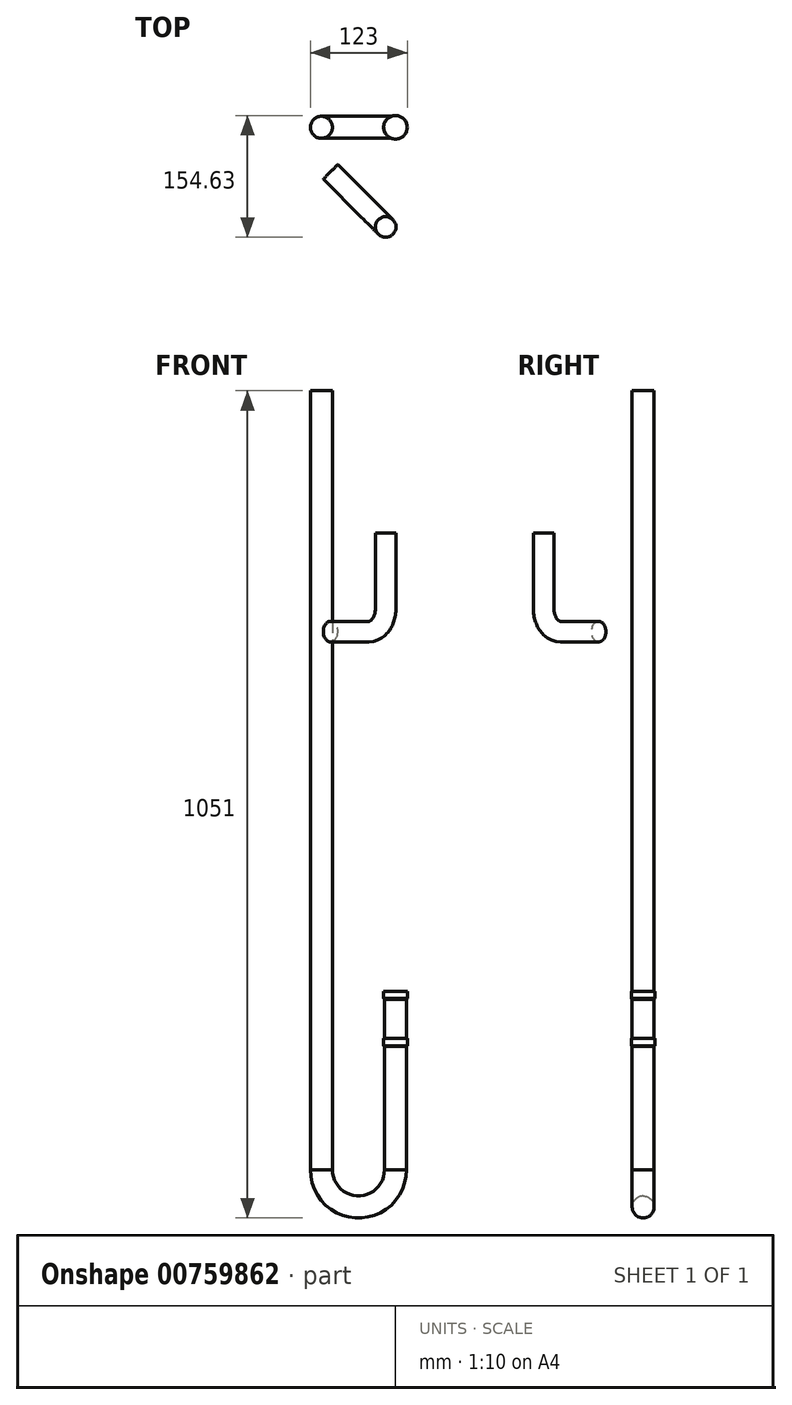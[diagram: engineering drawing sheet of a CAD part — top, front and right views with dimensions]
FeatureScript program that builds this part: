
annotation { "Feature Type Name" : "Feature", "Feature Type Description" : "" }
export const myFeature = defineFeature(function(context is Context, id is Id, definition is map)
    precondition{}
    {
        {
            var Q0;
            Q0=qCreatedBy(makeId("Top.planeOp"),FACE);
            cPlane(context, id + "F0", {"entities" : qUnion([Q0]), "cplaneType" : CPlaneType.OFFSET, "offset" : 302 * mm, "width" : 150 * mm, "height" : 150 * mm});
        }
        {
            var Q0;
            Q0=qCreatedBy(id+"F0.planeOp",FACE);
            var sketch = newSketch(context, id + "F1", { "sketchPlane" : qUnion([Q0])});
            skCircle(sketch, "E0", {"center": v(0, 0) * mm, "radius": 10 * mm});
            skSolve(sketch);
        }
        {
            var Q0;
            Q0=qCreatedBy(makeId("Front.planeOp"),FACE);
            var sketch = newSketch(context, id + "F2", { "sketchPlane" : qUnion([Q0])});
            skPoint(sketch, "E1.0", {"position": v(0, 302) * mm});
            skLineSegment(sketch, "E2", {"start": v(0, 302) * mm, "end": v(0, 75) * mm, "construction": true});
            skLineSegment(sketch, "E3", {"start": v(0, 75) * mm, "end": v(14, 75) * mm});
            skLineSegment(sketch, "E4", {"start": v(14, 75) * mm, "end": v(14, 232) * mm});
            skLineSegment(sketch, "E5", {"start": v(14, 232) * mm, "end": v(15, 232) * mm});
            skLineSegment(sketch, "E6", {"start": v(15, 232) * mm, "end": v(15, 242) * mm});
            skLineSegment(sketch, "E7", {"start": v(15, 242) * mm, "end": v(14, 242) * mm});
            skLineSegment(sketch, "E8", {"start": v(14, 242) * mm, "end": v(14, 292) * mm});
            skLineSegment(sketch, "E9", {"start": v(14, 292) * mm, "end": v(15, 292) * mm});
            skLineSegment(sketch, "E10", {"start": v(15, 292) * mm, "end": v(15, 302) * mm});
            skLineSegment(sketch, "E11", {"start": v(15, 302) * mm, "end": v(0, 302) * mm});
            skLineSegment(sketch, "E12", {"start": v(0, 75) * mm, "end": v(0, 302) * mm});
            skSolve(sketch);
        }
        {
            var Q0;
            Q0=makeQuery(id+"F2.imprint","IMPRINT",FACE,{"disambiguationData":[TD([[makeQuery(id+"F2.imprint","IMPRINT",EDGE,{"derivedFrom":sQuery(id+"F2.wireOp",EDGE,"E3")}),1.0]])]});
            var Q1;
            Q1=sQuery(id+"F2.wireOp",EDGE,"E12");
            revolve(context, id + "F3", {"surfaceOperationType" : NewSurfaceOperationType.NEW, "entities" : qUnion([Q0]), "axis" : qUnion([Q1]), "revolveType" : RevolveType.FULL});
        }
        {
            var Q0;
            Q0=makeQuery(id+"F3.opRevolve","SWEPT_EDGE",EDGE,{"disambiguationData":[OSD([sQuery(id+"F2.wireOp",EDGE,"E5"),sQuery(id+"F2.wireOp",EDGE,"E6")])]});
            var Q1;
            Q1=makeQuery(id+"F3.opRevolve","SWEPT_EDGE",EDGE,{"disambiguationData":[OSD([sQuery(id+"F2.wireOp",EDGE,"E9"),sQuery(id+"F2.wireOp",EDGE,"E10")])]});
            chamfer(context, id + "F4", {"entities" : qUnion([Q0, Q1]), "width" : 1 * mm, "tangentPropagation" : true});
        }
        {
            var Q0;
            Q0=qCreatedBy(makeId("Front.planeOp"),FACE);
            var sketch = newSketch(context, id + "F5", { "sketchPlane" : qUnion([Q0])});
            skLineSegment(sketch, "E13", {"start": v(-139, 389.52) * mm, "end": v(-139, -176.73) * mm, "construction": true});
            skLineSegment(sketch, "E14", {"start": v(-94, 348.15) * mm, "end": v(-94, 75) * mm, "construction": true});
            skLineSegment(sketch, "E15.0", {"start": v(14, 75) * mm, "end": v(-14, 75) * mm});
            skLineSegment(sketch, "E16", {"start": v(-14, 75) * mm, "end": v(-94, 75) * mm, "construction": true});
            skSolve(sketch);
        }
        {
            var Q0;
            Q0=makeQuery(id+"F3.opRevolve","SWEPT_FACE",FACE,{"disambiguationData":[OSD([sQuery(id+"F2.wireOp",EDGE,"E3")])]});
            var sketch = newSketch(context, id + "F6", { "sketchPlane" : qUnion([Q0])});
            skPoint(sketch, "E17.0", {"position": v(-94, 0) * mm});
            skCircle(sketch, "E18", {"center": v(-94, 0) * mm, "radius": 14 * mm});
            skCircle(sketch, "E19.0", {"center": v(0, 0) * mm, "radius": 14 * mm});
            skSolve(sketch);
        }
        {
            var Q0;
            Q0=makeQuery(id+"F6.imprint","IMPRINT",FACE,{"disambiguationData":[TD([[makeQuery(id+"F6.imprint","IMPRINT",EDGE,{"derivedFrom":sQuery(id+"F6.wireOp",EDGE,"E18")}),1.0]])]});
            extrude(context, id + "F7", {"entities" : qUnion([Q0]), "oppositeDirection" : true, "depth" : 990 * mm, "offsetDistance" : 25 * mm});
        }
        {
            var Q0;
            Q0=qCreatedBy(makeId("Front.planeOp"),FACE);
            var sketch = newSketch(context, id + "F8", { "sketchPlane" : qUnion([Q0])});
            skPoint(sketch, "E20.0", {"position": v(-94, 75) * mm});
            skPoint(sketch, "E21.0", {"position": v(0, 75) * mm});
            skArc(sketch, "E22", {"start": v(-94, 75) * mm, "mid": v(-47, 28) * mm, "end": v(0, 75) * mm});
            skSolve(sketch);
        }
        {
            var Q0;
            Q0=makeQuery(id+"F3.opRevolve","SWEPT_FACE",FACE,{"disambiguationData":[OSD([sQuery(id+"F2.wireOp",EDGE,"E3")])]});
            var Q1;
            Q1=sQuery(id+"F8.wireOp",EDGE,"E22");
            sweep(context, id + "F9", {"profiles" : qUnion([Q0]), "path" : qUnion([Q1])});
        }
        {
            var Q0;
            Q0=qCreatedBy(makeId("Top.planeOp"),FACE);
            cPlane(context, id + "F10", {"entities" : qUnion([Q0]), "cplaneType" : CPlaneType.OFFSET, "offset" : (889 - 5) * mm, "width" : 150 * mm, "height" : 150 * mm});
        }
        {
            var Q0;
            Q0=qCreatedBy(id+"F10.planeOp",FACE);
            var sketch = newSketch(context, id + "F11", { "sketchPlane" : qUnion([Q0])});
            skCircle(sketch, "E23", {"center": v(-12.43, -126.57) * mm, "radius": 13.06 * mm});
            skPoint(sketch, "E24.0", {"position": v(-139, 0) * mm});
            skLineSegment(sketch, "E25", {"start": v(-139, 0) * mm, "end": v(92.72, 0) * mm, "construction": true});
            skLineSegment(sketch, "E26", {"start": v(-139, 0) * mm, "end": v(0, -139) * mm, "construction": true});
            skSolve(sketch);
        }
        {
            var Q0;
            Q0=sQuery(id+"F11.wireOp",EDGE,"E26");
            cPlane(context, id + "F12", {"entities" : qUnion([Q0]), "cplaneType" : CPlaneType.LINE_ANGLE, "offset" : 25 * mm, "angle" : 90 * degree, "width" : 150 * mm, "height" : 150 * mm});
        }
        {
            var Q0;
            Q0=qCreatedBy(id+"F12.planeOp",FACE);
            var sketch = newSketch(context, id + "F13", { "sketchPlane" : qUnion([Q0])});
            skPoint(sketch, "E27.0", {"position": v(-80.71, 884) * mm});
            skLineSegment(sketch, "E28", {"start": v(-80.71, 884) * mm, "end": v(-80.71, 789) * mm});
            skLineSegment(sketch, "E29", {"start": v(-50.71, 759) * mm, "end": v(18.29, 759) * mm});
            skArc(sketch, "E30", {"start": v(-80.71, 789) * mm, "mid": v(-71.93, 767.79) * mm, "end": v(-50.71, 759) * mm});
            skSolve(sketch);
        }
        {
            var Q0;
            Q0=makeQuery(id+"F11.imprint","IMPRINT",FACE,{"disambiguationData":[TD([[makeQuery(id+"F11.imprint","IMPRINT",EDGE,{"derivedFrom":sQuery(id+"F11.wireOp",EDGE,"E23")}),1.0]])]});
            var Q1;
            Q1=sQuery(id+"F13.wireOp",EDGE,"E28");
            var Q2;
            Q2=sQuery(id+"F13.wireOp",EDGE,"E30");
            var Q3;
            Q3=sQuery(id+"F13.wireOp",EDGE,"E29");
            sweep(context, id + "F14", {"profiles" : qUnion([Q0]), "path" : qUnion([Q1, Q2, Q3])});
        }
    });
